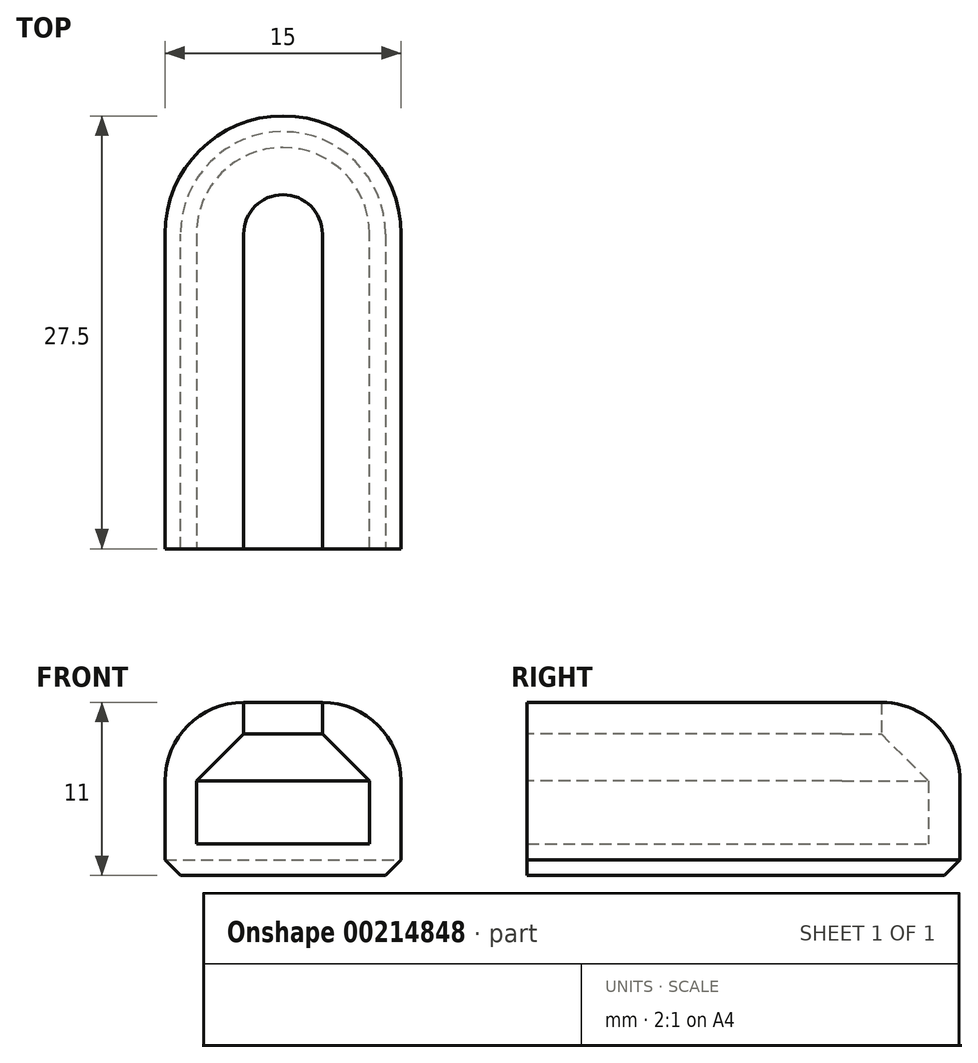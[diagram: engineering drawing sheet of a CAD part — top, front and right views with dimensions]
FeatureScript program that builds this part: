
annotation { "Feature Type Name" : "Feature", "Feature Type Description" : "" }
export const myFeature = defineFeature(function(context is Context, id is Id, definition is map)
    precondition{}
    {
        {
            var Q0;
            Q0=qCreatedBy(makeId("Front.planeOp"),FACE);
            var sketch = newSketch(context, id + "F0", { "sketchPlane" : qUnion([Q0])});
            skLineSegment(sketch, "E0", {"start": v(0, 0) * mm, "end": v(0, 6) * mm});
            skLineSegment(sketch, "E1", {"start": v(5, 11) * mm, "end": v(5, 11) * mm});
            skLineSegment(sketch, "E2.0", {"start": v(2, 6) * mm, "end": v(5, 9) * mm});
            skLineSegment(sketch, "E2.1", {"start": v(2, 0) * mm, "end": v(2, 6) * mm});
            skLineSegment(sketch, "E3", {"start": v(0, 0) * mm, "end": v(2, 0) * mm});
            skLineSegment(sketch, "E4", {"start": v(5, 11) * mm, "end": v(5, 9) * mm});
            skPoint(sketch, "E5.visualSharp", {"position": v(0, 11) * mm});
            skArc(sketch, "E5.filletArc", {"start": v(5, 11) * mm, "mid": v(1.46, 9.54) * mm, "end": v(0, 6) * mm});
            skSolve(sketch);
        }
        {
            var Q0;
            Q0=qCreatedBy(makeId("Top.planeOp"),FACE);
            var sketch = newSketch(context, id + "F1", { "sketchPlane" : qUnion([Q0])});
            skLineSegment(sketch, "E6", {"start": v(0, 0) * mm, "end": v(0, 20) * mm});
            skArc(sketch, "E7", {"start": v(0, 20) * mm, "mid": v(2.2, 25.3) * mm, "end": v(7.5, 27.5) * mm});
            skLineSegment(sketch, "E8", {"start": v(7.5, 27.5) * mm, "end": v(7.5, -15) * mm, "construction": true});
            skArc(sketch, "E9.MirrorCS", {"start": v(15, 20) * mm, "mid": v(12.8, 25.3) * mm, "end": v(7.5, 27.5) * mm});
            skLineSegment(sketch, "E10.MirrorCS", {"start": v(15, 0) * mm, "end": v(15, 20) * mm});
            skLineSegment(sketch, "E11", {"start": v(0, 0) * mm, "end": v(7.5, 0) * mm});
            skLineSegment(sketch, "E12.MirrorCS", {"start": v(15, 0) * mm, "end": v(7.5, 0) * mm});
            skSolve(sketch);
        }
        {
            var Q0;
            Q0=makeQuery(id+"F0.imprint","IMPRINT",FACE,{"disambiguationData":[TD([[makeQuery(id+"F0.imprint","IMPRINT",EDGE,{"derivedFrom":sQuery(id+"F0.wireOp",EDGE,"E0")}),-1.0]])]});
            var Q1;
            Q1=sQuery(id+"F1.wireOp",EDGE,"E6");
            var Q2;
            Q2=sQuery(id+"F1.wireOp",EDGE,"E7");
            var Q3;
            Q3=sQuery(id+"F1.wireOp",EDGE,"E9.MirrorCS");
            var Q4;
            Q4=sQuery(id+"F1.wireOp",EDGE,"E10.MirrorCS");
            sweep(context, id + "F2", {"profiles" : qUnion([Q0]), "path" : qUnion([Q1, Q2, Q3, Q4])});
        }
        {
            var Q0;
            Q0=makeQuery(id+"F1.imprint","IMPRINT",FACE,{"disambiguationData":[TD([[makeQuery(id+"F1.imprint","IMPRINT",EDGE,{"derivedFrom":sQuery(id+"F1.wireOp",EDGE,"E6")}),-1.0]])]});
            extrude(context, id + "F3", {"entities" : qUnion([Q0]), "operationType" : NewBodyOperationType.ADD, "depth" : 2 * mm});
        }
        {
            var Q0;
            Q0=makeQuery(id+"F2.opSweep","SWEPT_EDGE",EDGE,{"disambiguationData":[OSD([sQuery(id+"F0.wireOp",EDGE,"E0"),sQuery(id+"F0.wireOp",EDGE,"E3"),sQuery(id+"F1.wireOp",EDGE,"E6")])]});
            var Q1;
            Q1=makeQuery(id+"F2.opSweep","SWEPT_EDGE",EDGE,{"disambiguationData":[OSD([sQuery(id+"F0.wireOp",EDGE,"E0"),sQuery(id+"F0.wireOp",EDGE,"E3"),sQuery(id+"F1.wireOp",EDGE,"E7")])]});
            var Q2;
            Q2=makeQuery(id+"F2.opSweep","SWEPT_EDGE",EDGE,{"disambiguationData":[OSD([sQuery(id+"F0.wireOp",EDGE,"E0"),sQuery(id+"F0.wireOp",EDGE,"E3"),sQuery(id+"F1.wireOp",EDGE,"E10.MirrorCS")])]});
            chamfer(context, id + "F4", {"entities" : qUnion([Q0, Q1, Q2]), "width" : 1 * mm, "tangentPropagation" : true});
        }
    });
